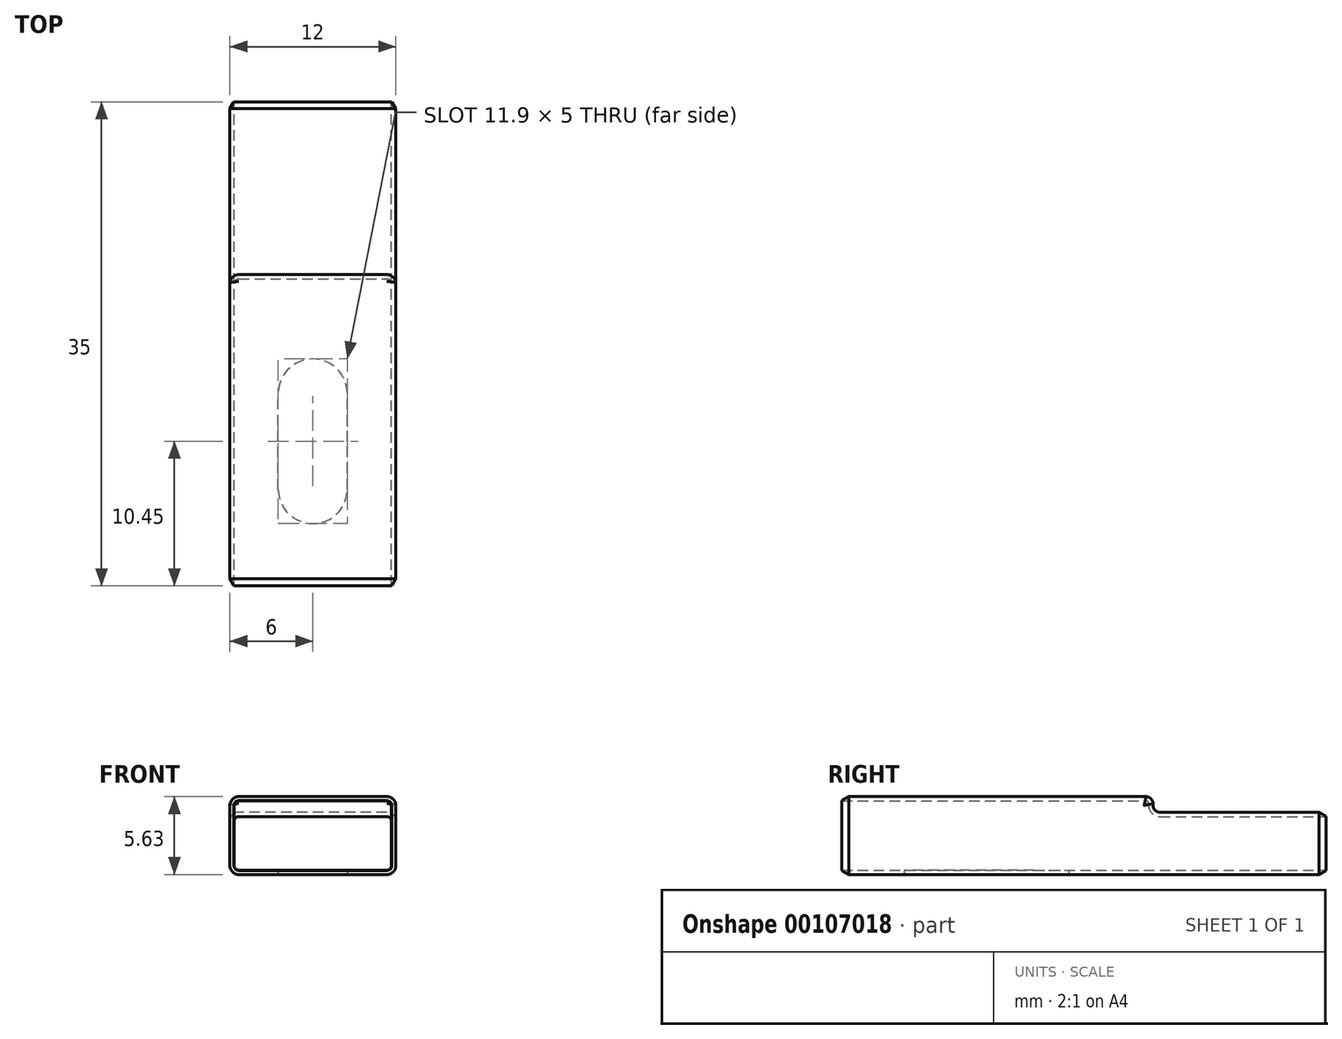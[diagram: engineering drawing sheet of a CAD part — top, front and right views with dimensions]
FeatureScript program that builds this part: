
annotation { "Feature Type Name" : "Feature", "Feature Type Description" : "" }
export const myFeature = defineFeature(function(context is Context, id is Id, definition is map)
    precondition{}
    {
        {
            var Q0;
            Q0=qCreatedBy(makeId("Right.planeOp"),FACE);
            var sketch = newSketch(context, id + "F0", { "sketchPlane" : qUnion([Q0])});
            skLineSegment(sketch, "E0.bottom", {"start": v(0, 0) * mm, "end": v(-12.5, 0) * mm});
            skLineSegment(sketch, "E0.top", {"start": v(0, 4.5) * mm, "end": v(-12.5, 4.5) * mm});
            skLineSegment(sketch, "E0.left", {"start": v(0, 0) * mm, "end": v(0, 4.5) * mm});
            skLineSegment(sketch, "E1.bottom", {"start": v(-12.5, 0) * mm, "end": v(-35, 0) * mm});
            skLineSegment(sketch, "E1.top", {"start": v(-12.5, 5.63) * mm, "end": v(-35, 5.63) * mm});
            skLineSegment(sketch, "E1.left", {"start": v(-12.5, 4.5) * mm, "end": v(-12.5, 5.63) * mm});
            skLineSegment(sketch, "E1.right", {"start": v(-35, 0) * mm, "end": v(-35, 5.63) * mm});
            skSolve(sketch);
        }
        {
            var Q0;
            Q0=makeQuery(id+"F0.imprint","IMPRINT",FACE,{"disambiguationData":[TD([[makeQuery(id+"F0.imprint","IMPRINT",EDGE,{"derivedFrom":sQuery(id+"F0.wireOp",EDGE,"E0.bottom")}),-1.0]])]});
            extrude(context, id + "F1", {"entities" : qUnion([Q0]), "depth" : 12 * mm, "symmetric" : true});
        }
        {
            var Q0;
            Q0=makeQuery(id+"F1.opExtrude","SWEPT_EDGE",EDGE,{"disambiguationData":[OSD([sQuery(id+"F0.wireOp",EDGE,"E0.top"),sQuery(id+"F0.wireOp",EDGE,"E1.left")])]});
            fillet(context, id + "F2", {"entities" : qUnion([Q0]), "radius" : .5 * mm, "tangentPropagation" : true, "allowEdgeOverflow" : false});
        }
        {
            var Q0;
            Q0=makeQuery(id+"F1.opExtrude","SWEPT_EDGE",EDGE,{"disambiguationData":[OSD([sQuery(id+"F0.wireOp",EDGE,"E1.top"),sQuery(id+"F0.wireOp",EDGE,"E1.left")])]});
            fillet(context, id + "F3", {"entities" : qUnion([Q0]), "radius" : .5 * mm, "tangentPropagation" : true, "allowEdgeOverflow" : false});
        }
        {
            var Q0;
            Q0=makeQuery(id+"F1.opExtrude","CAP_EDGE",EDGE,{"disambiguationData":[OSD([sQuery(id+"F0.wireOp",EDGE,"E0.top")])],"isStart":true});
            var Q1;
            Q1=makeQuery(id+"F1.opExtrude","CAP_EDGE",EDGE,{"disambiguationData":[OSD([sQuery(id+"F0.wireOp",EDGE,"E0.top")])],"isStart":false});
            var Q2;
            Q2=makeQuery(id+"F1.opExtrude","CAP_EDGE",EDGE,{"disambiguationData":[OSD([sQuery(id+"F0.wireOp",EDGE,"E0.bottom"),sQuery(id+"F0.wireOp",EDGE,"E1.bottom")])],"isStart":false});
            var Q3;
            Q3=makeQuery(id+"F1.opExtrude","CAP_EDGE",EDGE,{"disambiguationData":[OSD([sQuery(id+"F0.wireOp",EDGE,"E0.bottom"),sQuery(id+"F0.wireOp",EDGE,"E1.bottom")])],"isStart":true});
            fillet(context, id + "F4", {"entities" : qUnion([Q0, Q1, Q2, Q3]), "radius" : .64 * mm, "tangentPropagation" : true, "allowEdgeOverflow" : false});
        }
        {
            var Q0;
            Q0=makeQuery(id+"F1.opExtrude","SWEPT_FACE",FACE,{"disambiguationData":[OSD([sQuery(id+"F0.wireOp",EDGE,"E0.left")])]});
            var Q1;
            Q1=makeQuery(id+"F1.opExtrude","SWEPT_FACE",FACE,{"disambiguationData":[OSD([sQuery(id+"F0.wireOp",EDGE,"E1.right")])]});
            shell(context, id + "F5", {"entities" : qUnion([Q0, Q1]), "thickness" : .315 * mm});
        }
        {
            var Q0;
            Q0=makeQuery(id+"F1.opExtrude","SWEPT_EDGE",EDGE,{"disambiguationData":[OSD([sQuery(id+"F0.wireOp",EDGE,"E0.top"),sQuery(id+"F0.wireOp",EDGE,"E0.left")])]});
            chamfer(context, id + "F6", {"entities" : qUnion([Q0]), "chamferType" : ChamferType.OFFSET_ANGLE, "width" : .5 * mm, "oppositeDirection" : false, "angle" : 30 * degree, "tangentPropagation" : true});
        }
        {
            var Q0;
            Q0=makeQuery(id+"F1.opExtrude","SWEPT_EDGE",EDGE,{"disambiguationData":[OSD([sQuery(id+"F0.wireOp",EDGE,"E1.top"),sQuery(id+"F0.wireOp",EDGE,"E1.right")])]});
            chamfer(context, id + "F7", {"entities" : qUnion([Q0]), "chamferType" : ChamferType.OFFSET_ANGLE, "width" : .5 * mm, "oppositeDirection" : true, "angle" : 30 * degree, "tangentPropagation" : true});
        }
        {
            var Q0;
            Q0=makeQuery(id+"F1.opExtrude","SWEPT_FACE",FACE,{"disambiguationData":[OSD([sQuery(id+"F0.wireOp",EDGE,"E0.bottom"),sQuery(id+"F0.wireOp",EDGE,"E1.bottom")])]});
            var sketch = newSketch(context, id + "F8", { "sketchPlane" : qUnion([Q0])});
            skLineSegment(sketch, "E2", {"start": v(0, 35.56) * mm, "end": v(0, 17.14) * mm, "construction": true});
            skLineSegment(sketch, "E3.left", {"start": v(2.5, 28) * mm, "end": v(2.5, 21.1) * mm});
            skLineSegment(sketch, "E3.right", {"start": v(-2.5, 28) * mm, "end": v(-2.5, 21.1) * mm});
            skPoint(sketch, "E3.middle", {"position": v(0, 24.55) * mm});
            skArc(sketch, "E4", {"start": v(2.5, 28) * mm, "mid": v(0, 30.5) * mm, "end": v(-2.5, 28) * mm});
            skArc(sketch, "E5", {"start": v(2.5, 21.1) * mm, "mid": v(0, 18.6) * mm, "end": v(-2.5, 21.1) * mm});
            skSolve(sketch);
        }
        {
            var Q0;
            Q0 = qSketchRegion(id + "F8", true);
            extrude(context, id + "F9", {"entities" : qUnion([Q0]), "operationType" : NewBodyOperationType.REMOVE, "endBound" : BoundingType.UP_TO_NEXT, "oppositeDirection" : true, "depth" : 25 * mm});
        }
    });
